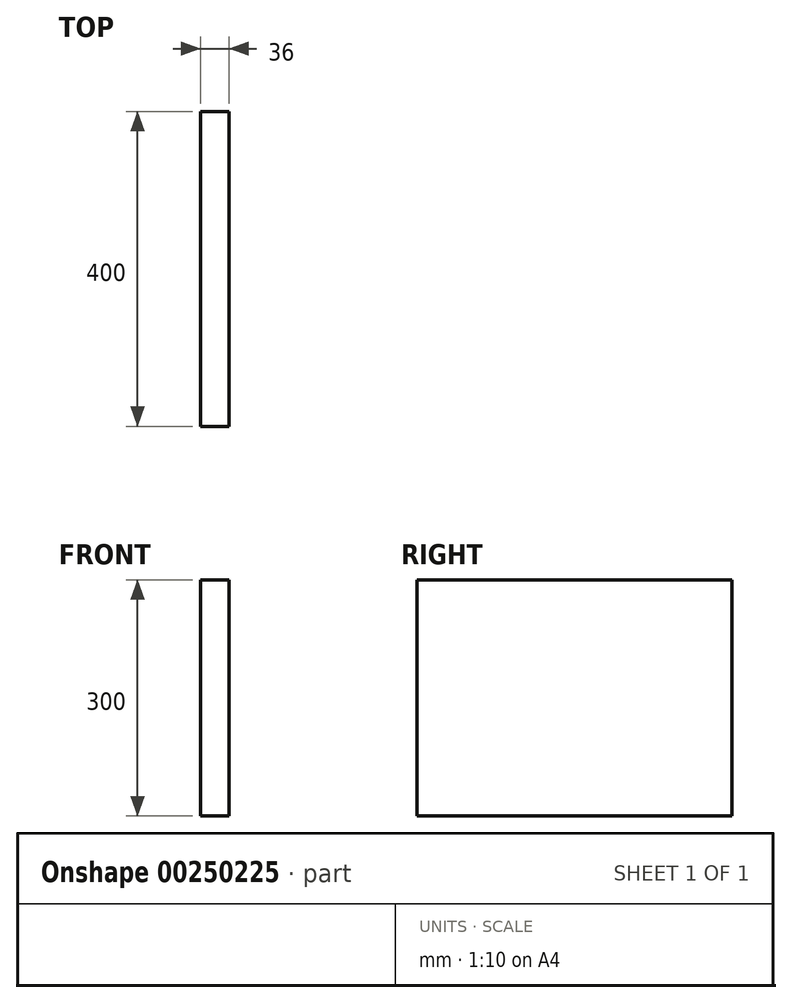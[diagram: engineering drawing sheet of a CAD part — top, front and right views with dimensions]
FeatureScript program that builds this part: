
annotation { "Feature Type Name" : "Feature", "Feature Type Description" : "" }
export const myFeature = defineFeature(function(context is Context, id is Id, definition is map)
    precondition{}
    {
        {
            var Q0;
            Q0=qCreatedBy(makeId("Front.planeOp"),FACE);
            var sketch = newSketch(context, id + "F0", { "sketchPlane" : qUnion([Q0])});
            skLineSegment(sketch, "E0.bottom", {"start": v(71.78, 140.75) * mm, "end": v(107.78, 140.75) * mm});
            skLineSegment(sketch, "E0.top", {"start": v(71.78, -159.25) * mm, "end": v(107.78, -159.25) * mm});
            skLineSegment(sketch, "E0.left", {"start": v(71.78, 140.75) * mm, "end": v(71.78, -159.25) * mm});
            skLineSegment(sketch, "E0.right", {"start": v(107.78, 140.75) * mm, "end": v(107.78, -159.25) * mm});
            skSolve(sketch);
        }
        {
            var Q0;
            Q0=makeQuery(id+"F0.imprint","IMPRINT",FACE,{"disambiguationData":[TD([[makeQuery(id+"F0.imprint","IMPRINT",EDGE,{"derivedFrom":sQuery(id+"F0.wireOp",EDGE,"E0.bottom")}),-1.0]])]});
            extrude(context, id + "F1", {"entities" : qUnion([Q0]), "depth" : 400 * mm});
        }
    });
